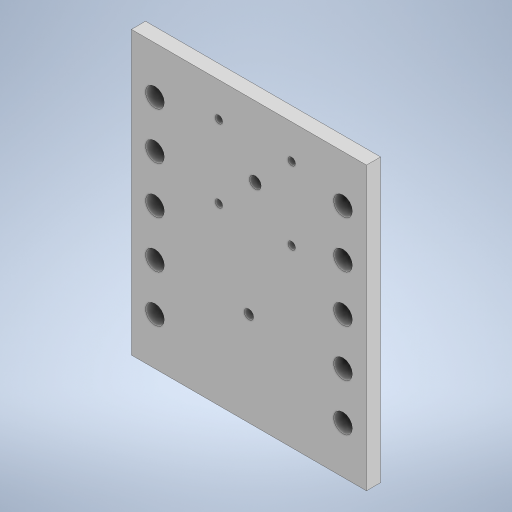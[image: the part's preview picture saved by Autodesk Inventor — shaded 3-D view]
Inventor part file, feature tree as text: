
AUTODESK INVENTOR PART (.ipt)
format: ipt  version: 2023 (Build 270158000, 158)  size: 265,216 bytes
history: native  units: mm
features: plane x1, extrude x1, sketch x1
ambient origin geometry x8: Origin, YZ Plane, XZ Plane, XY Plane, X Axis, Y Axis, Z Axis, Center Point
bodies: Solid1 (feature_tree)
feature tree (3):
  plane  "Work Plane1"
  extrude  "Extrusion1"  Depth=6.0mm
  sketch  "Sketch1"  dims[d0=4.0mm d1=5.0mm d2=40.0mm d3=50.0mm d4=120.0mm d5=100.0mm d6=3.2mm d7=3.2mm d8=3.2mm d9=3.2mm d10=10.0mm d11=20.0mm d12=20.0mm d13=20.0mm d14=20.0mm d15=20.0mm d16=10.0mm d17=20.0mm d18=20.0mm d19=20.0mm d20=20.0mm d21=20.0mm d22=8.0mm d23=8.0mm d24=8.0mm d25=8.0mm d26=8.0mm d27=8.0mm d28=8.0mm d29=8.0mm d30=8.0mm d31=8.0mm d32=6.0mm d33=0.0mm]
